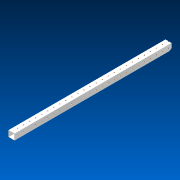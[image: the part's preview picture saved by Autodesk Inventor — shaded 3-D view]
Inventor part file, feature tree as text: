
AUTODESK INVENTOR PART (.ipt)
format: ipt  version: 2022.2 (Build 262287000, 287)  size: 873,984 bytes
history: native  units: in
note: dims shown in document units (in); Inventor stores cm internally (conversion verified against a paired STEP export)
features: other x52, extrude x2, pattern_linear x2, sketch x2
ambient origin geometry x8: Origin, YZ Plane, XZ Plane, XY Plane, X Axis, Y Axis, Z Axis, Center Point
bodies: Solid1 (feature_tree)
feature tree (58):
  extrude  "Extrusion1"  TaperAngle=0.0deg  [1 undecoded]
  other  "Work Axis1"
  other  "Work Axis2"
  pattern_linear  "Rectangular Pattern1"  Count1=26  [1 undecoded]
  pattern_linear  "Rectangular Pattern2"  Count1=25  [1 undecoded]
  extrude  "Extrusion2"  Depth=1.0in
  sketch  "Sketch1"  dims[d0=33.0in d1=0.0in d2=10.2362in]
  other  "Work Axis3"
  other  "Work Axis4"
  other  "Work Axis5"
  other  "Work Axis6"
  other  "Work Axis7"
  other  "Work Axis8"
  other  "Work Axis9"
  other  "Work Axis10"
  other  "Work Axis11"
  other  "Work Axis12"
  other  "Work Axis13"
  other  "Work Axis14"
  other  "Work Axis15"
  other  "Work Axis16"
  other  "Work Axis17"
  other  "Work Axis18"
  other  "Work Axis19"
  other  "Work Axis20"
  other  "Work Axis21"
  other  "Work Axis22"
  other  "Work Axis23"
  other  "Work Axis24"
  other  "Work Axis25"
  other  "Work Axis26"
  other  "Work Axis27"
  other  "Work Axis28"
  other  "Work Axis29"
  other  "Work Axis63"
  other  "Work Axis64"
  other  "Work Axis65"
  other  "Work Axis66"
  other  "Work Axis67"
  other  "Work Axis68"
  other  "Work Axis69"
  other  "Work Axis70"
  other  "Work Axis71"
  other  "Work Axis72"
  other  "Work Axis73"
  other  "Work Axis74"
  other  "Work Axis75"
  other  "Work Axis76"
  other  "Work Axis77"
  other  "Work Axis78"
  other  "Work Axis79"
  other  "Work Axis80"
  other  "Work Axis81"
  other  "Work Axis82"
  other  "Work Axis83"
  other  "Work Axis84"
  sketch  "Sketch2"  dims[d4=1.0in d5=9.8425in d7=1.0in d8=60.0deg d9=0.0in d10=0.0in]
  other  "LPattern2"
note: 3 required parameter values undecoded (feature->parameter linkage not recoverable at this tier; creation-order binding heuristic only, values carry confidence <= 0.55)
